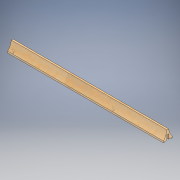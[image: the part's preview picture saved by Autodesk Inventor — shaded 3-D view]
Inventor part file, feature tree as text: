
AUTODESK INVENTOR PART (.ipt)
format: ipt  version: 2022.2 (Build 262287010, 287A)  size: 179,200 bytes
history: native  units: in
note: dims shown in document units (in); Inventor stores cm internally (conversion verified against a paired STEP export)
features: revolve x2, other x1, direct_edit x1
ambient origin geometry x8: Origin, YZ Plane, XZ Plane, XY Plane, X Axis, Y Axis, Z Axis, Center Point
bodies: Solid1 (feature_tree)
feature tree (4):
  other  "Mull (Lower)"
  direct_edit  "Direct Edit1"
  revolve  "Rotate1"  [1 undecoded]
  revolve  "Rotate2"  Angle=180.0deg
note: 1 required parameter value undecoded (feature->parameter linkage not recoverable at this tier; creation-order binding heuristic only, values carry confidence <= 0.55)
